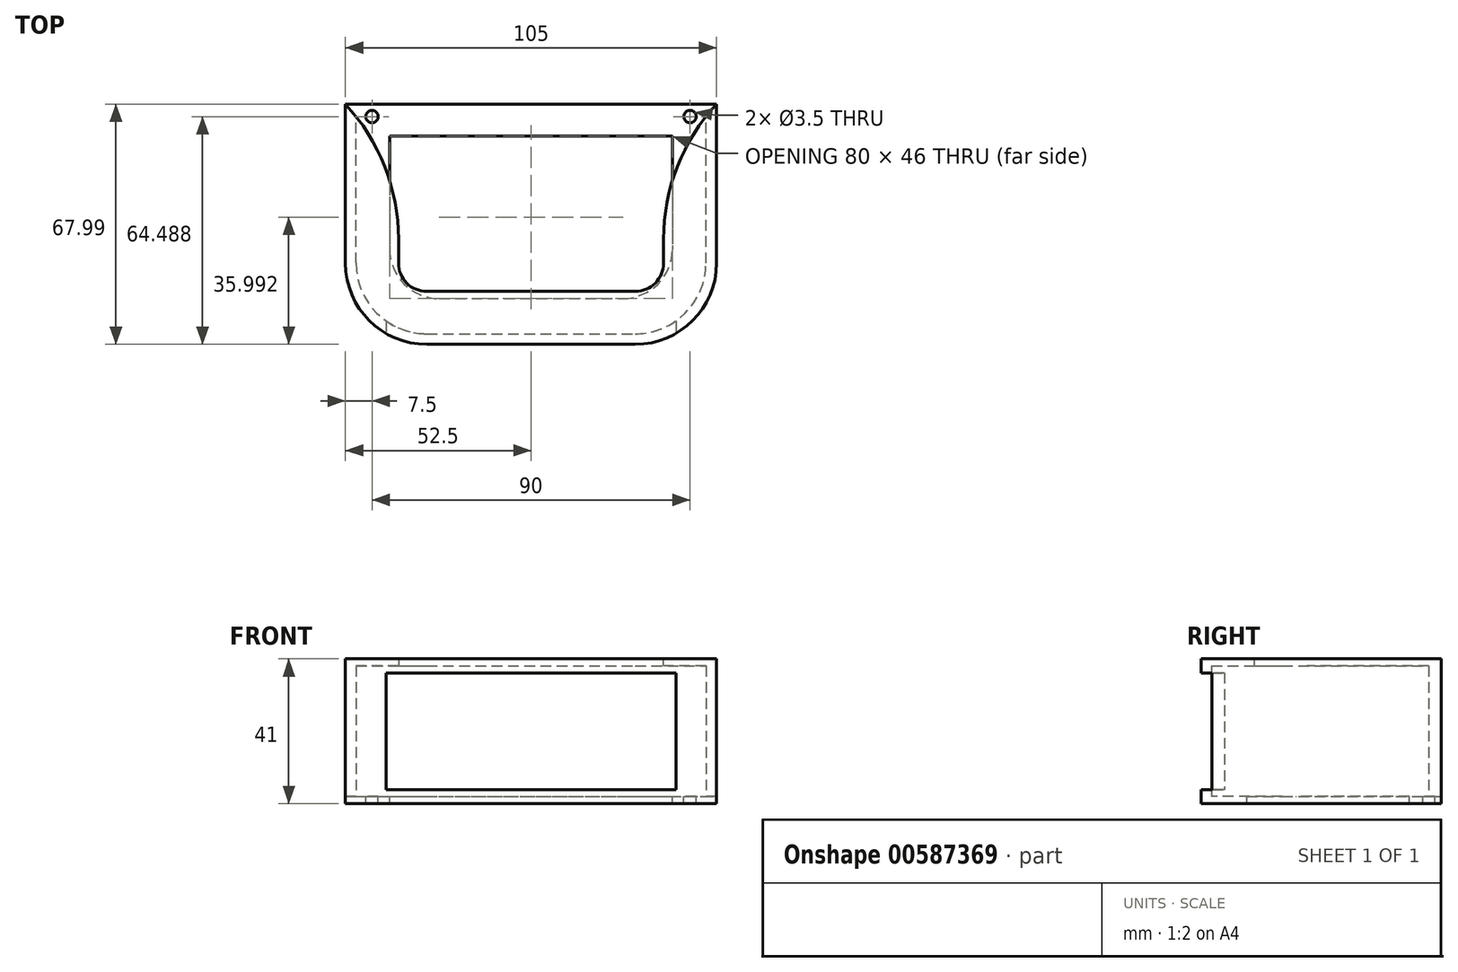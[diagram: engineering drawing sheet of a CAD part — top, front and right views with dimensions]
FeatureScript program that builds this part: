
annotation { "Feature Type Name" : "Feature", "Feature Type Description" : "" }
export const myFeature = defineFeature(function(context is Context, id is Id, definition is map)
    precondition{}
    {
        {
            var Q0;
            Q0=qCreatedBy(makeId("Top.planeOp"),FACE);
            var sketch = newSketch(context, id + "F0", { "sketchPlane" : qUnion([Q0])});
            skLineSegment(sketch, "E0.bottom", {"start": v(20, 0) * mm, "end": v(79, 0) * mm});
            skLineSegment(sketch, "E0.top", {"start": v(20, 104.7) * mm, "end": v(79, 104.7) * mm});
            skLineSegment(sketch, "E0.left", {"start": v(0, 20) * mm, "end": v(0, 84.7) * mm});
            skLineSegment(sketch, "E0.right", {"start": v(99, 20) * mm, "end": v(99, 84.7) * mm});
            skPoint(sketch, "E1.centerSnap0", {"position": v(0, 52.35) * mm});
            skPoint(sketch, "E1.centerSnap1", {"position": v(49.5, 104.7) * mm});
            skPoint(sketch, "E2.visualSharp", {"position": v(0, 104.7) * mm});
            skArc(sketch, "E2.filletArc", {"start": v(20, 104.7) * mm, "mid": v(5.86, 98.84) * mm, "end": v(0, 84.7) * mm});
            skPoint(sketch, "E3.visualSharp", {"position": v(99, 104.7) * mm});
            skArc(sketch, "E3.filletArc", {"start": v(99, 84.7) * mm, "mid": v(93.14, 98.84) * mm, "end": v(79, 104.7) * mm});
            skPoint(sketch, "E4.visualSharp", {"position": v(99, 0) * mm});
            skArc(sketch, "E4.filletArc", {"start": v(79, 0) * mm, "mid": v(93.14, 5.86) * mm, "end": v(99, 20) * mm});
            skPoint(sketch, "E5.visualSharp", {"position": v(0, 0) * mm});
            skArc(sketch, "E5.filletArc", {"start": v(0, 20) * mm, "mid": v(5.86, 5.86) * mm, "end": v(20, 0) * mm});
            skPoint(sketch, "E1.center.orphan", {"position": v(49.5, 52.35) * mm});
            skArc(sketch, "E6.0", {"start": v(20, 107.7) * mm, "mid": v(3.74, 100.96) * mm, "end": v(-3, 84.7) * mm});
            skLineSegment(sketch, "E6.1", {"start": v(-3, 20) * mm, "end": v(-3, 84.7) * mm});
            skLineSegment(sketch, "E6.2", {"start": v(20, 107.7) * mm, "end": v(79, 107.7) * mm});
            skArc(sketch, "E6.3", {"start": v(-3, 20) * mm, "mid": v(3.74, 3.74) * mm, "end": v(20, -3) * mm});
            skArc(sketch, "E6.4", {"start": v(102, 84.7) * mm, "mid": v(95.26, 100.96) * mm, "end": v(79, 107.7) * mm});
            skLineSegment(sketch, "E6.5", {"start": v(102, 20) * mm, "end": v(102, 84.7) * mm});
            skArc(sketch, "E6.6", {"start": v(79, -3) * mm, "mid": v(95.26, 3.74) * mm, "end": v(102, 20) * mm});
            skLineSegment(sketch, "E6.7", {"start": v(20, -3) * mm, "end": v(79, -3) * mm});
            skSolve(sketch);
        }
        {
            var Q0;
            Q0=makeQuery(id+"F0.imprint","IMPRINT",FACE,{"disambiguationData":[TD([[makeQuery(id+"F0.imprint","IMPRINT",EDGE,{"derivedFrom":sQuery(id+"F0.wireOp",EDGE,"E0.bottom")}),1.0]])]});
            extrude(context, id + "F1", {"entities" : qUnion([Q0]), "depth" : 2 * mm, "offsetDistance" : 25 * mm});
        }
        {
            var Q0;
            Q0 = qSketchRegion(id + "F0", true);
            extrude(context, id + "F2", {"entities" : qUnion([Q0]), "operationType" : NewBodyOperationType.ADD, "depth" : 39 * mm, "offsetDistance" : 25 * mm});
        }
        {
            var Q0;
            Q0=makeQuery(id+"F2.opExtrude","CAP_FACE",FACE,{"disambiguationData":[OSD([sQuery(id+"F0.wireOp",EDGE,"E0.bottom"),sQuery(id+"F0.wireOp",EDGE,"E0.top"),sQuery(id+"F0.wireOp",EDGE,"E0.left"),sQuery(id+"F0.wireOp",EDGE,"E0.right"),sQuery(id+"F0.wireOp",EDGE,"E2.filletArc"),sQuery(id+"F0.wireOp",EDGE,"E3.filletArc"),sQuery(id+"F0.wireOp",EDGE,"E4.filletArc"),sQuery(id+"F0.wireOp",EDGE,"E5.filletArc"),sQuery(id+"F0.wireOp",EDGE,"E6.0"),sQuery(id+"F0.wireOp",EDGE,"E6.1"),sQuery(id+"F0.wireOp",EDGE,"E6.2"),sQuery(id+"F0.wireOp",EDGE,"E6.3"),sQuery(id+"F0.wireOp",EDGE,"E6.4"),sQuery(id+"F0.wireOp",EDGE,"E6.5"),sQuery(id+"F0.wireOp",EDGE,"E6.6"),sQuery(id+"F0.wireOp",EDGE,"E6.7")])],"isStart":false});
            var sketch = newSketch(context, id + "F3", { "sketchPlane" : qUnion([Q0])});
            skLineSegment(sketch, "E7.bottom", {"start": v(-11.09, 65) * mm, "end": v(111.34, 65) * mm});
            skLineSegment(sketch, "E7.top", {"start": v(-11.09, 113.96) * mm, "end": v(111.34, 113.96) * mm});
            skLineSegment(sketch, "E7.left", {"start": v(-11.09, 65) * mm, "end": v(-11.09, 113.96) * mm});
            skLineSegment(sketch, "E7.right", {"start": v(111.34, 65) * mm, "end": v(111.34, 113.96) * mm});
            skSolve(sketch);
        }
        {
            var Q0;
            Q0 = qSketchRegion(id + "F3", true);
            extrude(context, id + "F4", {"entities" : qUnion([Q0]), "operationType" : NewBodyOperationType.REMOVE, "endBound" : BoundingType.THROUGH_ALL, "oppositeDirection" : true, "depth" : 25 * mm, "offsetDistance" : 25 * mm});
        }
        {
            var Q0;
            Q0=makeQuery(id+"F1.opExtrude","CAP_FACE",FACE,{"disambiguationData":[OSD([sQuery(id+"F0.wireOp",EDGE,"E0.bottom"),sQuery(id+"F0.wireOp",EDGE,"E0.top"),sQuery(id+"F0.wireOp",EDGE,"E0.left"),sQuery(id+"F0.wireOp",EDGE,"E0.right"),sQuery(id+"F0.wireOp",EDGE,"E2.filletArc"),sQuery(id+"F0.wireOp",EDGE,"E3.filletArc"),sQuery(id+"F0.wireOp",EDGE,"E4.filletArc"),sQuery(id+"F0.wireOp",EDGE,"E5.filletArc")])],"isStart":false});
            var sketch = newSketch(context, id + "F5", { "sketchPlane" : qUnion([Q0])});
            skLineSegment(sketch, "E8.bottom", {"start": v(9.5, 56) * mm, "end": v(89.5, 56) * mm});
            skLineSegment(sketch, "E8.top", {"start": v(23.5, 10) * mm, "end": v(75.5, 10) * mm});
            skLineSegment(sketch, "E8.left", {"start": v(9.5, 56) * mm, "end": v(9.5, 24) * mm});
            skLineSegment(sketch, "E8.right", {"start": v(89.5, 56) * mm, "end": v(89.5, 24) * mm});
            skLineSegment(sketch, "E9", {"start": v(49.5, 56) * mm, "end": v(49.5, 10) * mm});
            skPoint(sketch, "E10.visualSharp", {"position": v(9.5, 10) * mm});
            skArc(sketch, "E10.filletArc", {"start": v(9.5, 24) * mm, "mid": v(13.6, 14.1) * mm, "end": v(23.5, 10) * mm});
            skPoint(sketch, "E11.visualSharp", {"position": v(89.5, 10) * mm});
            skArc(sketch, "E11.filletArc", {"start": v(75.5, 10) * mm, "mid": v(85.4, 14.1) * mm, "end": v(89.5, 24) * mm});
            skSolve(sketch);
        }
        {
            var Q0;
            Q0 = qSketchRegion(id + "F5", true);
            extrude(context, id + "F6", {"entities" : qUnion([Q0]), "operationType" : NewBodyOperationType.REMOVE, "endBound" : BoundingType.THROUGH_ALL, "oppositeDirection" : true, "depth" : 25 * mm, "offsetDistance" : 25 * mm});
        }
        {
            var Q0;
            Q0=makeQuery(id+"F2.opExtrude","CAP_FACE",FACE,{"disambiguationData":[OSD([sQuery(id+"F0.wireOp",EDGE,"E0.bottom"),sQuery(id+"F0.wireOp",EDGE,"E0.top"),sQuery(id+"F0.wireOp",EDGE,"E0.left"),sQuery(id+"F0.wireOp",EDGE,"E0.right"),sQuery(id+"F0.wireOp",EDGE,"E2.filletArc"),sQuery(id+"F0.wireOp",EDGE,"E3.filletArc"),sQuery(id+"F0.wireOp",EDGE,"E4.filletArc"),sQuery(id+"F0.wireOp",EDGE,"E5.filletArc"),sQuery(id+"F0.wireOp",EDGE,"E6.0"),sQuery(id+"F0.wireOp",EDGE,"E6.1"),sQuery(id+"F0.wireOp",EDGE,"E6.2"),sQuery(id+"F0.wireOp",EDGE,"E6.3"),sQuery(id+"F0.wireOp",EDGE,"E6.4"),sQuery(id+"F0.wireOp",EDGE,"E6.5"),sQuery(id+"F0.wireOp",EDGE,"E6.6"),sQuery(id+"F0.wireOp",EDGE,"E6.7")])],"isStart":false});
            var sketch = newSketch(context, id + "F7", { "sketchPlane" : qUnion([Q0])});
            skLineSegment(sketch, "E12.0", {"start": v(12, 20) * mm, "end": v(12, 65) * mm});
            skLineSegment(sketch, "E12.1", {"start": v(87, 20) * mm, "end": v(87, 65) * mm});
            skArc(sketch, "E12.2", {"start": v(79, 12) * mm, "mid": v(84.66, 14.34) * mm, "end": v(87, 20) * mm});
            skLineSegment(sketch, "E12.3", {"start": v(20, 12) * mm, "end": v(79, 12) * mm});
            skArc(sketch, "E12.4", {"start": v(12, 20) * mm, "mid": v(14.34, 14.34) * mm, "end": v(20, 12) * mm});
            skLineSegment(sketch, "E13.0", {"start": v(-3, 20) * mm, "end": v(-3, 65) * mm});
            skLineSegment(sketch, "E13.1", {"start": v(102, 20) * mm, "end": v(102, 65) * mm});
            skArc(sketch, "E13.2", {"start": v(79, -3) * mm, "mid": v(95.26, 3.74) * mm, "end": v(102, 20) * mm});
            skLineSegment(sketch, "E13.3", {"start": v(20, -3) * mm, "end": v(79, -3) * mm});
            skArc(sketch, "E13.4", {"start": v(-3, 20) * mm, "mid": v(3.74, 3.74) * mm, "end": v(20, -3) * mm});
            skLineSegment(sketch, "E14", {"start": v(-3, 65) * mm, "end": v(12, 65) * mm});
            skLineSegment(sketch, "E15", {"start": v(87, 65) * mm, "end": v(102, 65) * mm});
            skSolve(sketch);
        }
        {
            var Q0;
            Q0 = qSketchRegion(id + "F7", true);
            extrude(context, id + "F8", {"entities" : qUnion([Q0]), "operationType" : NewBodyOperationType.ADD, "depth" : 2 * mm, "offsetDistance" : 25 * mm});
        }
        {
            var Q0;
            Q0=makeQuery(id+"F8.opExtrude","SWEPT_EDGE",EDGE,{"disambiguationData":[OSD([sQuery(id+"F7.wireOp",EDGE,"E12.0"),sQuery(id+"F7.wireOp",EDGE,"E14")])]});
            var Q1;
            Q1=makeQuery(id+"F8.opExtrude","SWEPT_EDGE",EDGE,{"disambiguationData":[OSD([sQuery(id+"F7.wireOp",EDGE,"E12.1"),sQuery(id+"F7.wireOp",EDGE,"E15")])]});
            fillet(context, id + "F9", {"entities" : qUnion([Q0, Q1]), "radius" : 56 * mm, "tangentPropagation" : true, "allowEdgeOverflow" : false});
        }
        {
            var Q0;
            Q0=makeQuery(id+"F8.boolean.opBoolean","MERGE",FACE,{"derivedFrom":[makeQuery(id+"F2.opExtrude","SWEPT_FACE",FACE,{"disambiguationData":[OSD([sQuery(id+"F0.wireOp",EDGE,"E6.7")])]}),makeQuery(id+"F8.opExtrude","SWEPT_FACE",FACE,{"disambiguationData":[OSD([sQuery(id+"F7.wireOp",EDGE,"E13.3")])]})]});
            var sketch = newSketch(context, id + "F10", { "sketchPlane" : qUnion([Q0])});
            skLineSegment(sketch, "E16.bottom", {"start": v(90.52, 37) * mm, "end": v(8.48, 37) * mm});
            skLineSegment(sketch, "E16.top", {"start": v(90.52, 4) * mm, "end": v(8.48, 4) * mm});
            skLineSegment(sketch, "E16.left", {"start": v(90.52, 37) * mm, "end": v(90.52, 4) * mm});
            skLineSegment(sketch, "E16.right", {"start": v(8.48, 37) * mm, "end": v(8.48, 4) * mm});
            skPoint(sketch, "E16.middle", {"position": v(49.5, 20.5) * mm});
            skPoint(sketch, "E16.middle.positionSnap0", {"position": v(20, 20.5) * mm});
            skPoint(sketch, "E16.middle.positionSnap1", {"position": v(49.5, 41) * mm});
            skPoint(sketch, "E16.centerSnap0", {"position": v(20, 20.5) * mm});
            skPoint(sketch, "E16.centerSnap1", {"position": v(49.5, 41) * mm});
            skSolve(sketch);
        }
        {
            var Q0;
            Q0 = qSketchRegion(id + "F10", true);
            extrude(context, id + "F11", {"entities" : qUnion([Q0]), "operationType" : NewBodyOperationType.REMOVE, "oppositeDirection" : true, "depth" : 25 * mm, "offsetDistance" : 25 * mm});
        }
        {
            var Q0;
            Q0=makeQuery(id+"F1.opExtrude","CAP_FACE",FACE,{"disambiguationData":[OSD([sQuery(id+"F0.wireOp",EDGE,"E0.bottom"),sQuery(id+"F0.wireOp",EDGE,"E0.top"),sQuery(id+"F0.wireOp",EDGE,"E0.left"),sQuery(id+"F0.wireOp",EDGE,"E0.right"),sQuery(id+"F0.wireOp",EDGE,"E2.filletArc"),sQuery(id+"F0.wireOp",EDGE,"E3.filletArc"),sQuery(id+"F0.wireOp",EDGE,"E4.filletArc"),sQuery(id+"F0.wireOp",EDGE,"E5.filletArc")])],"isStart":false});
            var sketch = newSketch(context, id + "F12", { "sketchPlane" : qUnion([Q0])});
            skCircle(sketch, "E17", {"center": v(94.5, 61.49) * mm, "radius": 1.75 * mm});
            skCircle(sketch, "E18", {"center": v(4.5, 61.49) * mm, "radius": 1.75 * mm});
            skPoint(sketch, "E19.center.orphan", {"position": v(9.5, 61.49) * mm});
            skPoint(sketch, "E20.center.orphan", {"position": v(89.5, 61.49) * mm});
            skSolve(sketch);
        }
        {
            var Q0;
            Q0 = qSketchRegion(id + "F12", true);
            extrude(context, id + "F13", {"entities" : qUnion([Q0]), "operationType" : NewBodyOperationType.REMOVE, "endBound" : BoundingType.THROUGH_ALL, "oppositeDirection" : true, "depth" : 25 * mm, "offsetDistance" : 25 * mm});
        }
    });
